# Revit family: ESHL-L-180-xxx-840-SMx
name_source: partatom
category: Oprawy oświetleniowe
revit_build: Autodesk Revit 2017 (Build: 20190507_1515(x64)
units: mm (PartAtom-declared; Revit-internal decimal feet)

## family parameters
Numer OmniClass = 23.80.70.11
Obiekt nadrzędny = Powierzchnia
Punkt obliczania pomieszczeń = Nie
Tnij formami wycięć po wczytaniu = Nie
Typ części = Normalny
Tytuł OmniClass = Luminaries for Internal Lighting
Współdzielony = Nie
Wymiar okrągłego złącza = Użyj średnicy
Źródło światła = Tak

## types (4) — shared parameters
Emituj kształt widoczny w renderingu = Nie
Emituj z długości prostokąta = 129 mm  [stored 0.423228 ft]
Emituj z szerokości prostokąta = 1496 mm  [stored 4.90814 ft]
Filtr koloru = 16777215
Kod zespołu = D5020200
Lampa = LED
Odchylenie kierunku = 90.00°
Producent = RIDI Leuchten GmbH
URL = www.ridi.de
Zmiana temperatury barwowej przyciemniania lampy = <Brak>
brand = RIDI
conformity mark = CE
electrical safety class = 1
height = 89 mm  [stored 0.291995 ft]
ingress protection (IP) code = IP40
length = 1548 mm  [stored 5.07874 ft]
nominal frequency = 50-60Hz
nominal voltage = 230
voltage type (AC, DC, UC) = AC
weight = 8,7 kg
width = 185 mm  [stored 0.606955 ft]
zero-valued in all types: Domyślna rzędna

## per-type parameters (varying)
| type | Model | Obciążenie pozorne | Plik sieci fotometrycznej | rated input power |
| ESHL-L 180/620-840 SM | 0850593 | 48 VA | ESHL-L 180620-840 SM.IES | 48 |
| ESHL-L 180/620-840 SM-DA | 0860593 | 48 VA | ESHL-L 180620-840 SM.IES | 48 |
| ESHL-L 180/935-840 SM | 0850626 | 70 VA | ESHL-L 180935-840 SM.IES | 70 |
| ESHL-L 180/935-840 SM-DA | 0860626 | 70 VA | ESHL-L 180935-840 SM.IES | 70 |

note: column(s) folded — value = type name in every type: product name

note: [stored X ft] marks values corroborated as IEEE doubles in the binary element streams (Revit-internal decimal feet)
